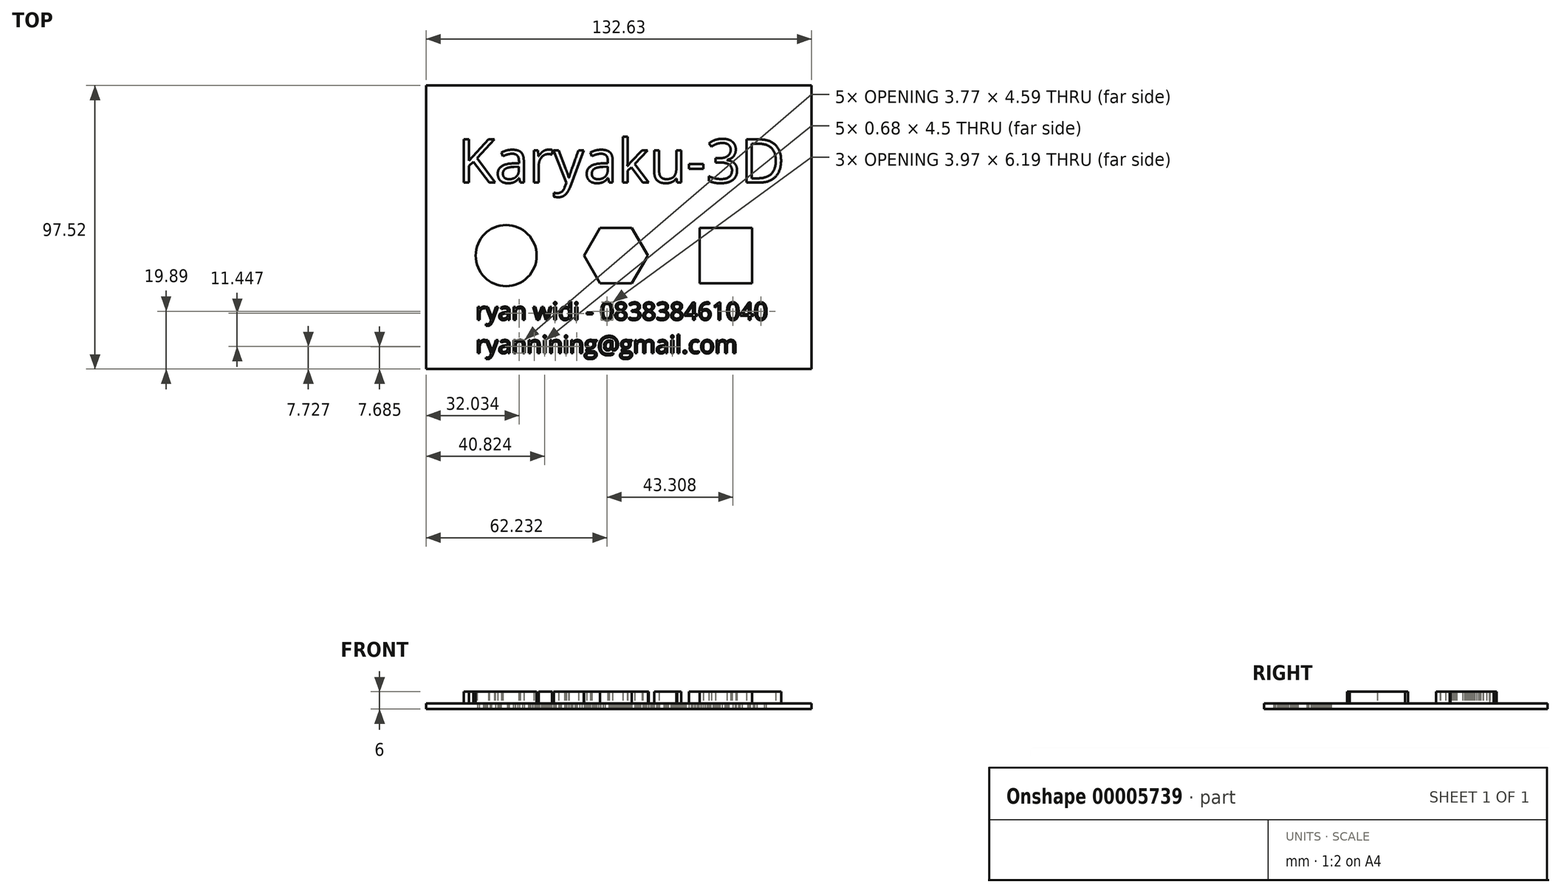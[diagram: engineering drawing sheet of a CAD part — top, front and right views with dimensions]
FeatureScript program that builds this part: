
annotation { "Feature Type Name" : "Feature", "Feature Type Description" : "" }
export const myFeature = defineFeature(function(context is Context, id is Id, definition is map)
    precondition{}
    {
        {
            var Q0;
            Q0=qCreatedBy(makeId("Top.planeOp"),FACE);
            var sketch = newSketch(context, id + "F0", { "sketchPlane" : qUnion([Q0])});
            skLineSegment(sketch, "E0.bottom", {"start": v(-79.27, 56.26) * mm, "end": v(53.36, 56.26) * mm});
            skLineSegment(sketch, "E0.top", {"start": v(-79.27, -41.26) * mm, "end": v(53.36, -41.26) * mm});
            skLineSegment(sketch, "E0.left", {"start": v(-79.27, 56.26) * mm, "end": v(-79.27, -41.26) * mm});
            skLineSegment(sketch, "E0.right", {"start": v(53.36, 56.26) * mm, "end": v(53.36, -41.26) * mm});
            skSolve(sketch);
        }
        {
            var Q0;
            Q0=makeQuery(id+"F0.imprint","IMPRINT",FACE,{"disambiguationData":[TD([[makeQuery(id+"F0.imprint","IMPRINT",EDGE,{"derivedFrom":sQuery(id+"F0.wireOp",EDGE,"E0.bottom")}),-1.0]])]});
            extrude(context, id + "F1", {"entities" : qUnion([Q0]), "oppositeDirection" : true, "depth" : 2 * mm});
        }
        {
            var Q0;
            Q0=qCreatedBy(makeId("Top.planeOp"),FACE);
            var sketch = newSketch(context, id + "F2", { "sketchPlane" : qUnion([Q0])});
            skText(sketch, "E1", { "text": "Karyaku-3D", "fontName": "OpenSans-Regular.ttf"});
            const initialGuessF2  = {"E1": [-0.06836, 0.02285, 1, 0, 0.015]};
            skSetInitialGuess(sketch, initialGuessF2);
            skSolve(sketch);
        }
        {
            var Q0;
            Q0 = qSketchRegion(id + "F2", true);
            extrude(context, id + "F3", {"entities" : qUnion([Q0]), "depth" : 4 * mm});
        }
        {
            var Q0;
            {var subQ0=sQuery(id+"F0.wireOp",EDGE,"E0.bottom");var subQ1=sQuery(id+"F0.wireOp",EDGE,"E0.top");var subQ2=sQuery(id+"F0.wireOp",EDGE,"E0.left");var subQ3=sQuery(id+"F0.wireOp",EDGE,"E0.right");Q0=makeQuery(id+"F3.boolean.opBoolean","SPLIT",FACE,{"disambiguationData":[TD([makeQuery(id+"F1.opExtrude","SWEPT_FACE",FACE,{"disambiguationData":[OSD([subQ0])]})])],"derivedFrom":makeQuery(id+"F1.opExtrude","CAP_FACE",FACE,{"disambiguationData":[OSD([subQ0,subQ1,subQ2,subQ3])],"isStart":true})});}
            var sketch = newSketch(context, id + "F4", { "sketchPlane" : qUnion([Q0])});
            skCircle(sketch, "E2", {"center": v(-51.73, -2.25) * mm, "radius": 10.5 * mm});
            skCircle(sketch, "E3.cCircle", {"center": v(-13.96, -2.25) * mm, "radius": 9.5 * mm, "construction": true});
            skLineSegment(sketch, "E3.0", {"start": v(-19.45, 7.25) * mm, "end": v(-8.48, 7.25) * mm});
            skLineSegment(sketch, "E3.1", {"start": v(-8.48, 7.25) * mm, "end": v(-3, -2.25) * mm});
            skLineSegment(sketch, "E3.2", {"start": v(-3, -2.25) * mm, "end": v(-8.48, -11.75) * mm});
            skLineSegment(sketch, "E3.3", {"start": v(-8.48, -11.75) * mm, "end": v(-19.45, -11.75) * mm});
            skLineSegment(sketch, "E3.4", {"start": v(-19.45, -11.75) * mm, "end": v(-24.93, -2.25) * mm});
            skLineSegment(sketch, "E3.5", {"start": v(-24.93, -2.25) * mm, "end": v(-19.45, 7.25) * mm});
            skPoint(sketch, "E3.0.midPoint", {"position": v(-13.96, 7.25) * mm});
            skLineSegment(sketch, "E4.bottom", {"start": v(-79.27, -41.26) * mm, "end": v(-74.07, -41.26) * mm});
            skLineSegment(sketch, "E4.top", {"start": v(-79.27, -35.44) * mm, "end": v(-74.07, -35.44) * mm});
            skLineSegment(sketch, "E4.left", {"start": v(-79.27, -41.26) * mm, "end": v(-79.27, -35.44) * mm});
            skLineSegment(sketch, "E4.right", {"start": v(-74.07, -41.26) * mm, "end": v(-74.07, -35.44) * mm});
            skLineSegment(sketch, "E5.bottom", {"start": v(53.36, -41.26) * mm, "end": v(46.86, -41.26) * mm});
            skLineSegment(sketch, "E5.top", {"start": v(53.36, -35.44) * mm, "end": v(46.86, -35.44) * mm});
            skLineSegment(sketch, "E5.left", {"start": v(53.36, -41.26) * mm, "end": v(53.36, -35.44) * mm});
            skLineSegment(sketch, "E5.right", {"start": v(46.86, -41.26) * mm, "end": v(46.86, -35.44) * mm});
            skLineSegment(sketch, "E6.rect.bottom", {"start": v(32.82, 7.25) * mm, "end": v(14.8, 7.25) * mm});
            skLineSegment(sketch, "E6.rect.top", {"start": v(32.82, -11.75) * mm, "end": v(14.8, -11.75) * mm});
            skLineSegment(sketch, "E6.rect.left", {"start": v(32.82, 7.25) * mm, "end": v(32.82, -11.75) * mm});
            skLineSegment(sketch, "E6.rect.right", {"start": v(14.8, 7.25) * mm, "end": v(14.8, -11.75) * mm});
            skPoint(sketch, "E6.rect.middle", {"position": v(23.8, -2.25) * mm});
            skSolve(sketch);
        }
        {
            var Q0;
            Q0=makeQuery(id+"F4.imprint","IMPRINT",FACE,{"disambiguationData":[TD([[makeQuery(id+"F4.imprint","IMPRINT",EDGE,{"derivedFrom":sQuery(id+"F4.wireOp",EDGE,"E2")}),1.0]])]});
            var Q1;
            Q1=makeQuery(id+"F4.imprint","IMPRINT",FACE,{"disambiguationData":[TD([[makeQuery(id+"F4.imprint","IMPRINT",EDGE,{"derivedFrom":sQuery(id+"F4.wireOp",EDGE,"E3.0")}),-1.0]])]});
            var Q2;
            Q2=makeQuery(id+"F4.imprint","IMPRINT",FACE,{"disambiguationData":[TD([[makeQuery(id+"F4.imprint","IMPRINT",EDGE,{"derivedFrom":sQuery(id+"F4.wireOp",EDGE,"E6.rect.bottom")}),1.0]])]});
            extrude(context, id + "F5", {"entities" : qUnion([Q0, Q1, Q2]), "depth" : 4 * mm});
        }
        {
            var Q0;
            Q0=makeQuery(id+"F4.imprint","IMPRINT",FACE,{"disambiguationData":[TD([[makeQuery(id+"F4.imprint","IMPRINT",EDGE,{"derivedFrom":sQuery(id+"F4.wireOp",EDGE,"E2")}),-1.0]])]});
            var sketch = newSketch(context, id + "F6", { "sketchPlane" : qUnion([Q0])});
            skText(sketch, "E7", { "text": "ryan widi - 083838461040\<email>", "fontName": "OpenSans-Regular.ttf"});
            const initialGuessF6  = {"E7": [-0.0622, -0.02438, 1, 0, 0.00606]};
            skSetInitialGuess(sketch, initialGuessF6);
            skSolve(sketch);
        }
        {
            var Q0;
            Q0 = qSketchRegion(id + "F6", true);
            extrude(context, id + "F7", {"entities" : qUnion([Q0]), "operationType" : NewBodyOperationType.REMOVE, "oppositeDirection" : true, "depth" : 25 * mm});
        }
    });
